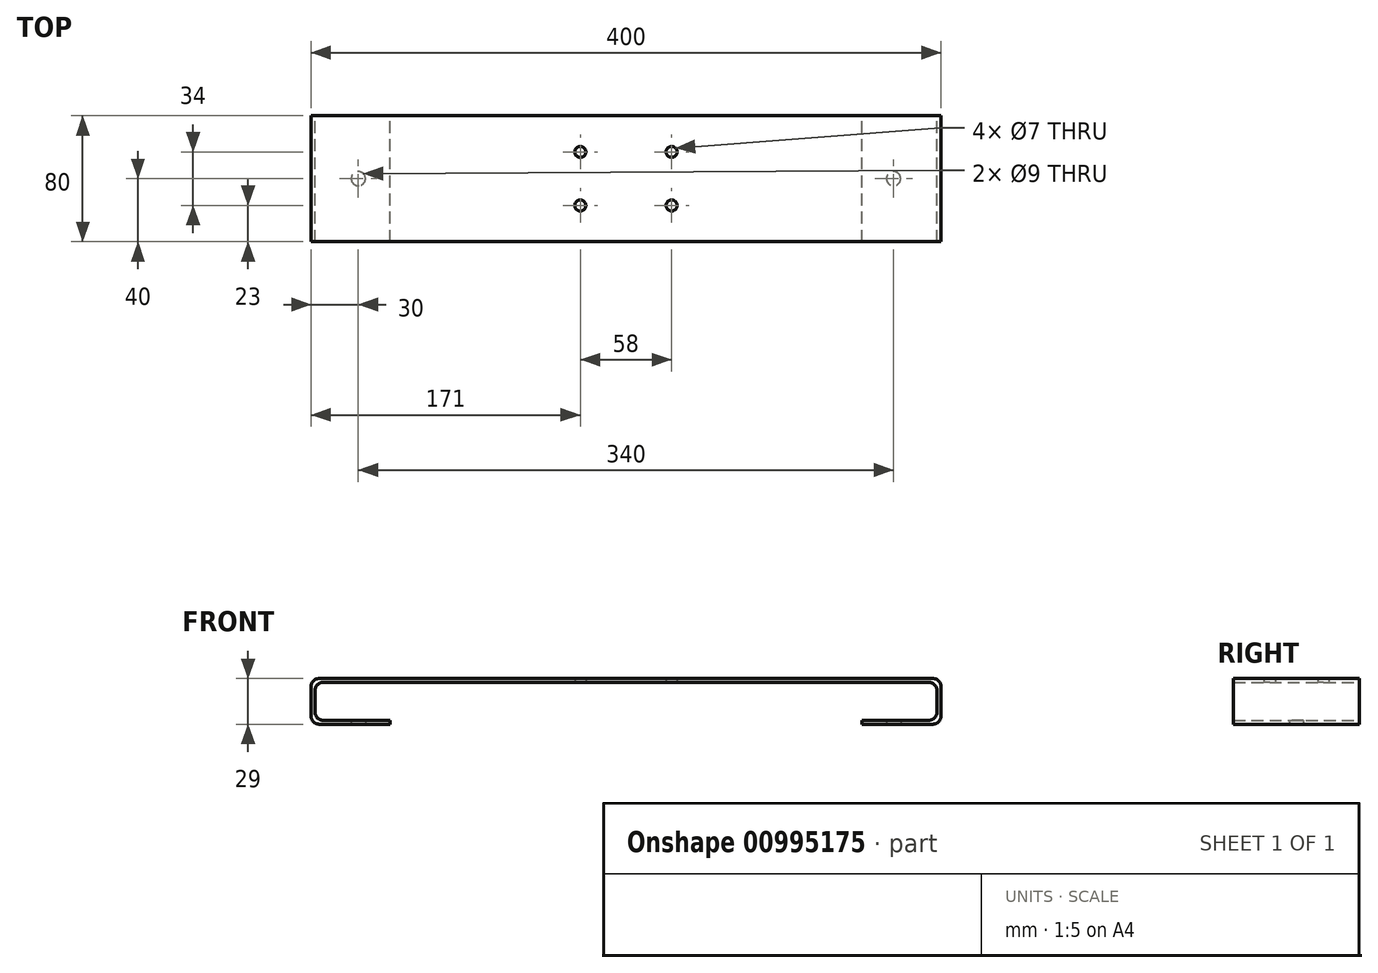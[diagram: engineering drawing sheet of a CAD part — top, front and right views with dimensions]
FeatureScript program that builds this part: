
annotation { "Feature Type Name" : "Feature", "Feature Type Description" : "" }
export const myFeature = defineFeature(function(context is Context, id is Id, definition is map)
    precondition{}
    {
        {
            var Q0;
            Q0=qCreatedBy(makeId("Front.planeOp"),FACE);
            var sketch = newSketch(context, id + "F0", { "sketchPlane" : qUnion([Q0])});
            skLineSegment(sketch, "E0", {"start": v(0, 0) * mm, "end": v(50, 0) * mm});
            skLineSegment(sketch, "E1", {"start": v(0, 0) * mm, "end": v(0, 29) * mm});
            skLineSegment(sketch, "E2", {"start": v(0, 29) * mm, "end": v(400, 29) * mm});
            skLineSegment(sketch, "E3", {"start": v(400, 29) * mm, "end": v(400, 0) * mm});
            skLineSegment(sketch, "E4", {"start": v(400, 0) * mm, "end": v(350, 0) * mm});
            skLineSegment(sketch, "E5.0", {"start": v(2.5, 2.5) * mm, "end": v(50, 2.5) * mm});
            skLineSegment(sketch, "E5.1", {"start": v(397.5, 2.5) * mm, "end": v(350, 2.5) * mm});
            skLineSegment(sketch, "E5.2", {"start": v(397.5, 26.5) * mm, "end": v(397.5, 2.5) * mm});
            skLineSegment(sketch, "E5.3", {"start": v(2.5, 26.5) * mm, "end": v(397.5, 26.5) * mm});
            skLineSegment(sketch, "E5.4", {"start": v(2.5, 2.5) * mm, "end": v(2.5, 26.5) * mm});
            skLineSegment(sketch, "E6", {"start": v(50, 2.5) * mm, "end": v(50, 0) * mm});
            skLineSegment(sketch, "E7", {"start": v(350, 2.5) * mm, "end": v(350, 0) * mm});
            skSolve(sketch);
        }
        {
            var Q0;
            Q0=qSketchRegion(id+"F0",true);
            extrude(context, id + "F1", {"entities" : qUnion([Q0]), "depth" : 80 * mm, "offsetDistance" : 25 * mm, "symmetric" : true});
        }
        {
            var Q0;
            Q0=makeQuery(id+"F1.opExtrude","SWEPT_FACE",FACE,{"disambiguationData":[OSD([sQuery(id+"F0.wireOp",EDGE,"E5.0")])]});
            var sketch = newSketch(context, id + "F2", { "sketchPlane" : qUnion([Q0])});
            skLineSegment(sketch, "E8", {"start": v(50, 0) * mm, "end": v(30, 0) * mm});
            skSolve(sketch);
        }
        {
            var Q0;
            Q0=makeQuery(id+"F1.opExtrude","SWEPT_FACE",FACE,{"disambiguationData":[OSD([sQuery(id+"F0.wireOp",EDGE,"E5.1")])]});
            var sketch = newSketch(context, id + "F3", { "sketchPlane" : qUnion([Q0])});
            skLineSegment(sketch, "E9", {"start": v(350, 0) * mm, "end": v(370, 0) * mm});
            skSolve(sketch);
        }
        {
            var Q0;
            Q0=sQuery(id+"F3.wireOp",VERTEX,"E9.end");
            var Q1;
            Q1=makeQuery(id+"F1.opExtrude","SWEPT_BODY",BODY,{"disambiguationData":[OSD([sQuery(id+"F0.wireOp",EDGE,"E0"),sQuery(id+"F0.wireOp",EDGE,"E1"),sQuery(id+"F0.wireOp",EDGE,"E2"),sQuery(id+"F0.wireOp",EDGE,"E3"),sQuery(id+"F0.wireOp",EDGE,"E4"),sQuery(id+"F0.wireOp",EDGE,"E5.0"),sQuery(id+"F0.wireOp",EDGE,"E5.1"),sQuery(id+"F0.wireOp",EDGE,"E5.2"),sQuery(id+"F0.wireOp",EDGE,"E5.3"),sQuery(id+"F0.wireOp",EDGE,"E5.4"),sQuery(id+"F0.wireOp",EDGE,"E6"),sQuery(id+"F0.wireOp",EDGE,"E7")])]});
            hole(context, id + "F4", {"style" : HoleStyle.SIMPLE, "endStyle" : HoleEndStyle.BLIND, "holeDiameter" : 9 * mm, "majorDiameter" : 5 * mm, "holeDepth" : 12 * mm, "isTappedThrough" : true, "tappedDepth" : 12 * mm, "tapClearance" : 3, "locations" : qUnion([Q0]), "scope" : qUnion([Q1]), "startStyle" : HoleStartStyle.PART});
        }
        {
            var Q0;
            Q0=sQuery(id+"F2.wireOp",VERTEX,"E8.end");
            var Q1;
            Q1=makeQuery(id+"F1.opExtrude","SWEPT_BODY",BODY,{"disambiguationData":[OSD([sQuery(id+"F0.wireOp",EDGE,"E0"),sQuery(id+"F0.wireOp",EDGE,"E1"),sQuery(id+"F0.wireOp",EDGE,"E2"),sQuery(id+"F0.wireOp",EDGE,"E3"),sQuery(id+"F0.wireOp",EDGE,"E4"),sQuery(id+"F0.wireOp",EDGE,"E5.0"),sQuery(id+"F0.wireOp",EDGE,"E5.1"),sQuery(id+"F0.wireOp",EDGE,"E5.2"),sQuery(id+"F0.wireOp",EDGE,"E5.3"),sQuery(id+"F0.wireOp",EDGE,"E5.4"),sQuery(id+"F0.wireOp",EDGE,"E6"),sQuery(id+"F0.wireOp",EDGE,"E7")])]});
            hole(context, id + "F5", {"style" : HoleStyle.SIMPLE, "endStyle" : HoleEndStyle.BLIND, "holeDiameter" : 9 * mm, "majorDiameter" : 5 * mm, "holeDepth" : 12 * mm, "isTappedThrough" : true, "tappedDepth" : 12 * mm, "tapClearance" : 3, "locations" : qUnion([Q0]), "scope" : qUnion([Q1]), "startStyle" : HoleStartStyle.PART});
        }
        {
            var Q0;
            Q0=makeQuery(id+"F1.opExtrude","SWEPT_FACE",FACE,{"disambiguationData":[OSD([sQuery(id+"F0.wireOp",EDGE,"E2")])]});
            var sketch = newSketch(context, id + "F6", { "sketchPlane" : qUnion([Q0])});
            skLineSegment(sketch, "E10", {"start": v(200, 40) * mm, "end": v(200, -40) * mm, "construction": true});
            skLineSegment(sketch, "E11", {"start": v(0, 0) * mm, "end": v(200, 0) * mm});
            skLineSegment(sketch, "E12.bottom", {"start": v(171, 17) * mm, "end": v(229, 17) * mm});
            skLineSegment(sketch, "E12.top", {"start": v(171, -17) * mm, "end": v(229, -17) * mm});
            skLineSegment(sketch, "E12.left", {"start": v(171, 17) * mm, "end": v(171, -17) * mm});
            skLineSegment(sketch, "E12.right", {"start": v(229, 17) * mm, "end": v(229, -17) * mm});
            skPoint(sketch, "E12.middle", {"position": v(200, 0) * mm});
            skSolve(sketch);
        }
        {
            var Q0;
            Q0=sQuery(id+"F6.wireOp",VERTEX,"E12.left.start");
            var Q1;
            Q1=sQuery(id+"F6.wireOp",VERTEX,"E12.right.start");
            var Q2;
            Q2=sQuery(id+"F6.wireOp",VERTEX,"E12.top.end");
            var Q3;
            Q3=sQuery(id+"F6.wireOp",VERTEX,"E12.left.end");
            var Q4;
            Q4=makeQuery(id+"F1.opExtrude","SWEPT_BODY",BODY,{"disambiguationData":[OSD([sQuery(id+"F0.wireOp",EDGE,"E0"),sQuery(id+"F0.wireOp",EDGE,"E1"),sQuery(id+"F0.wireOp",EDGE,"E2"),sQuery(id+"F0.wireOp",EDGE,"E3"),sQuery(id+"F0.wireOp",EDGE,"E4"),sQuery(id+"F0.wireOp",EDGE,"E5.0"),sQuery(id+"F0.wireOp",EDGE,"E5.1"),sQuery(id+"F0.wireOp",EDGE,"E5.2"),sQuery(id+"F0.wireOp",EDGE,"E5.3"),sQuery(id+"F0.wireOp",EDGE,"E5.4"),sQuery(id+"F0.wireOp",EDGE,"E6"),sQuery(id+"F0.wireOp",EDGE,"E7")])]});
            hole(context, id + "F7", {"style" : HoleStyle.SIMPLE, "endStyle" : HoleEndStyle.THROUGH, "holeDiameter" : 7 * mm, "majorDiameter" : 5 * mm, "isTappedThrough" : true, "tappedDepth" : 12 * mm, "tapClearance" : 3, "locations" : qUnion([Q0, Q1, Q2, Q3]), "scope" : qUnion([Q4]), "startStyle" : HoleStartStyle.PART});
        }
        {
            var Q0;
            Q0=makeQuery(id+"F1.opExtrude","SWEPT_EDGE",EDGE,{"disambiguationData":[OSD([sQuery(id+"F0.wireOp",EDGE,"E1"),sQuery(id+"F0.wireOp",EDGE,"E2")])]});
            var Q1;
            Q1=makeQuery(id+"F1.opExtrude","SWEPT_EDGE",EDGE,{"disambiguationData":[OSD([sQuery(id+"F0.wireOp",EDGE,"E0"),sQuery(id+"F0.wireOp",EDGE,"E1")])]});
            var Q2;
            Q2=makeQuery(id+"F1.opExtrude","SWEPT_EDGE",EDGE,{"disambiguationData":[OSD([sQuery(id+"F0.wireOp",EDGE,"E2"),sQuery(id+"F0.wireOp",EDGE,"E3")])]});
            var Q3;
            Q3=makeQuery(id+"F1.opExtrude","SWEPT_EDGE",EDGE,{"disambiguationData":[OSD([sQuery(id+"F0.wireOp",EDGE,"E3"),sQuery(id+"F0.wireOp",EDGE,"E4")])]});
            var Q4;
            Q4=makeQuery(id+"F1.opExtrude","SWEPT_EDGE",EDGE,{"disambiguationData":[OSD([sQuery(id+"F0.wireOp",EDGE,"E5.0"),sQuery(id+"F0.wireOp",EDGE,"E5.4")])]});
            var Q5;
            Q5=makeQuery(id+"F1.opExtrude","SWEPT_EDGE",EDGE,{"disambiguationData":[OSD([sQuery(id+"F0.wireOp",EDGE,"E5.3"),sQuery(id+"F0.wireOp",EDGE,"E5.4")])]});
            var Q6;
            Q6=makeQuery(id+"F1.opExtrude","SWEPT_EDGE",EDGE,{"disambiguationData":[OSD([sQuery(id+"F0.wireOp",EDGE,"E5.1"),sQuery(id+"F0.wireOp",EDGE,"E5.2")])]});
            var Q7;
            Q7=makeQuery(id+"F1.opExtrude","SWEPT_EDGE",EDGE,{"disambiguationData":[OSD([sQuery(id+"F0.wireOp",EDGE,"E5.2"),sQuery(id+"F0.wireOp",EDGE,"E5.3")])]});
            fillet(context, id + "F8", {"entities" : qUnion([Q0, Q1, Q2, Q3, Q4, Q5, Q6, Q7]), "radius" : 5 * mm, "tangentPropagation" : true, "allowEdgeOverflow" : false});
        }
    });
